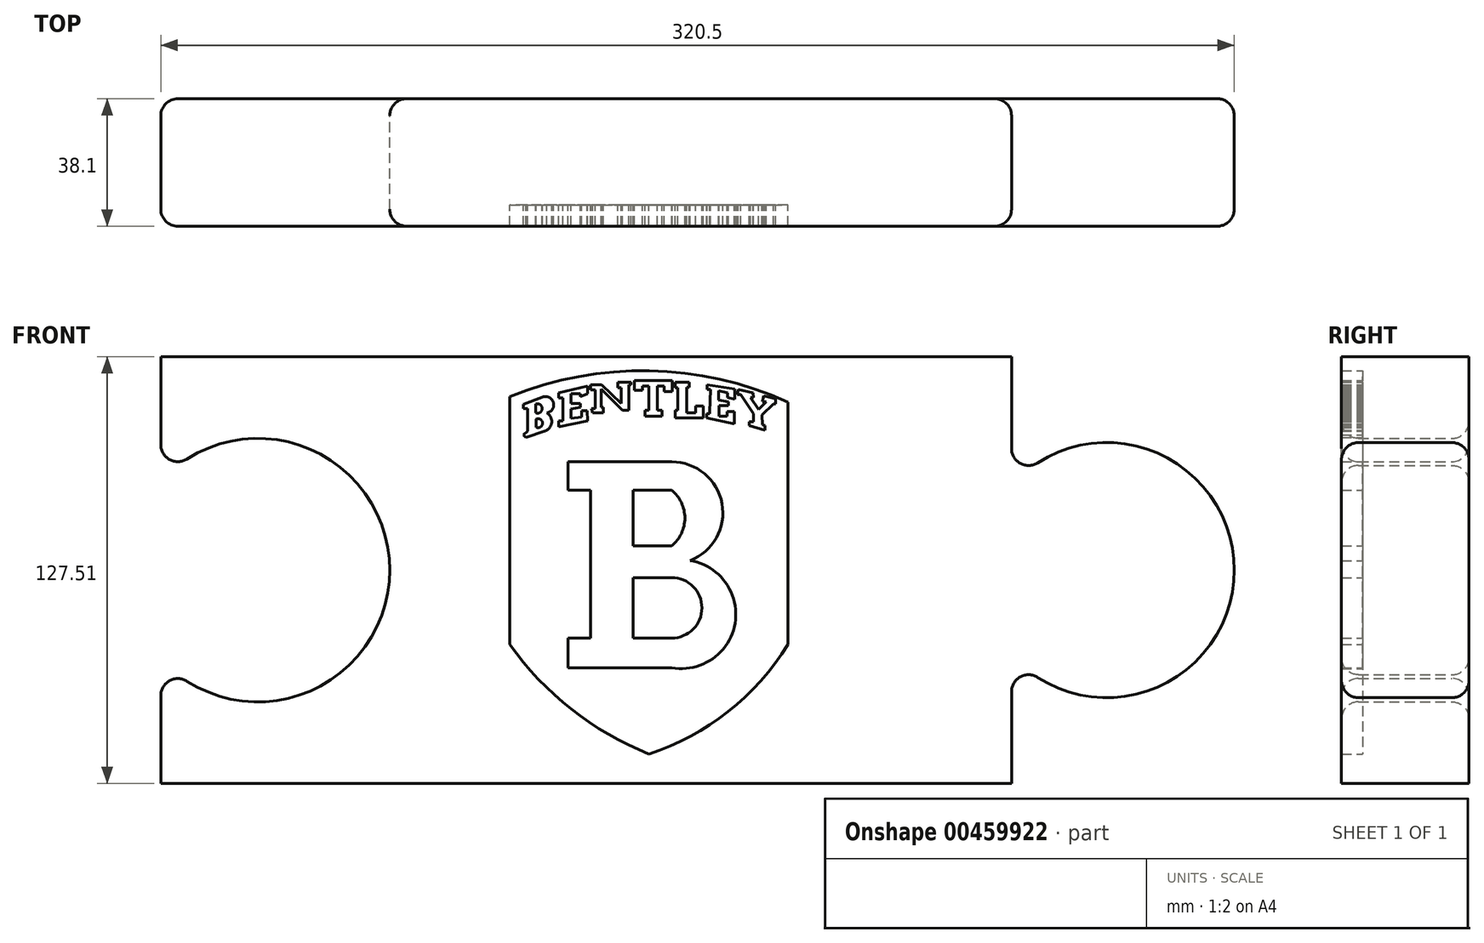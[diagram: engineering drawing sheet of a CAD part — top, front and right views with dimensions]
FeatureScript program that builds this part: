
annotation { "Feature Type Name" : "Feature", "Feature Type Description" : "" }
export const myFeature = defineFeature(function(context is Context, id is Id, definition is map)
    precondition{}
    {
        {
            var Q0;
            Q0=qCreatedBy(makeId("Front.planeOp"),FACE);
            var sketch = newSketch(context, id + "F0", { "sketchPlane" : qUnion([Q0])});
            skLineSegment(sketch, "E0", {"start": v(209.2, -174.77) * mm, "end": v(463.2, -174.77) * mm});
            skLineSegment(sketch, "E1", {"start": v(209.2, -302.28) * mm, "end": v(463.2, -302.28) * mm});
            skArc(sketch, "E2", {"start": v(463.2, -263.93) * mm, "mid": v(529.7, -238.53) * mm, "end": v(463.2, -213.13) * mm});
            skLineSegment(sketch, "E3", {"start": v(463.2, -213.13) * mm, "end": v(463.2, -174.77) * mm});
            skLineSegment(sketch, "E4", {"start": v(463.2, -263.93) * mm, "end": v(463.2, -302.28) * mm});
            skArc(sketch, "E5", {"start": v(209.2, -265.2) * mm, "mid": v(277.52, -238.53) * mm, "end": v(209.2, -211.86) * mm});
            skLineSegment(sketch, "E6", {"start": v(209.2, -265.2) * mm, "end": v(209.2, -302.28) * mm});
            skLineSegment(sketch, "E7", {"start": v(209.2, -211.86) * mm, "end": v(209.2, -174.77) * mm});
            skLineSegment(sketch, "E8", {"start": v(313.38, -186.66) * mm, "end": v(313.38, -260.76) * mm});
            skLineSegment(sketch, "E9", {"start": v(396.41, -188.31) * mm, "end": v(396.41, -260.76) * mm});
            skArc(sketch, "E10", {"start": v(396.41, -188.31) * mm, "mid": v(355.06, -178.97) * mm, "end": v(313.38, -186.66) * mm});
            skArc(sketch, "E11", {"start": v(313.38, -260.76) * mm, "mid": v(331.78, -280.1) * mm, "end": v(354.9, -293.46) * mm});
            skArc(sketch, "E12", {"start": v(354.9, -293.46) * mm, "mid": v(378.58, -280.83) * mm, "end": v(396.41, -260.76) * mm});
            skLineSegment(sketch, "E13", {"start": v(330.94, -206.94) * mm, "end": v(330.94, -216.88) * mm});
            skLineSegment(sketch, "E14", {"start": v(330.94, -206.94) * mm, "end": v(362.4, -206.94) * mm});
            skLineSegment(sketch, "E15", {"start": v(330.94, -216.88) * mm, "end": v(337.57, -216.88) * mm});
            skLineSegment(sketch, "E16", {"start": v(337.57, -216.88) * mm, "end": v(337.57, -259.1) * mm});
            skLineSegment(sketch, "E17", {"start": v(337.57, -259.1) * mm, "end": v(330.94, -259.1) * mm});
            skLineSegment(sketch, "E18", {"start": v(330.94, -259.1) * mm, "end": v(330.94, -269.04) * mm});
            skLineSegment(sketch, "E19", {"start": v(330.94, -269.04) * mm, "end": v(365.3, -269.04) * mm});
            skLineSegment(sketch, "E20", {"start": v(350.4, -241.72) * mm, "end": v(350.4, -258.62) * mm});
            skLineSegment(sketch, "E21", {"start": v(350.4, -241.72) * mm, "end": v(359.92, -241.72) * mm});
            skLineSegment(sketch, "E22", {"start": v(350.4, -215.64) * mm, "end": v(350.4, -230.95) * mm});
            skLineSegment(sketch, "E23", {"start": v(350.4, -215.64) * mm, "end": v(359.92, -215.64) * mm});
            skLineSegment(sketch, "E24", {"start": v(350.4, -230.95) * mm, "end": v(359.92, -230.95) * mm});
            skArc(sketch, "E25", {"start": v(359.92, -230.95) * mm, "mid": v(367.58, -223.3) * mm, "end": v(359.92, -215.64) * mm});
            skArc(sketch, "E26", {"start": v(359.92, -258.62) * mm, "mid": v(368.37, -250.17) * mm, "end": v(359.92, -241.72) * mm});
            skArc(sketch, "E27", {"start": v(366.54, -235.5) * mm, "mid": v(376.84, -219.43) * mm, "end": v(362.4, -206.94) * mm});
            skArc(sketch, "E28", {"start": v(365.3, -269.04) * mm, "mid": v(382.08, -252.87) * mm, "end": v(366.54, -235.5) * mm});
            skLineSegment(sketch, "E29", {"start": v(350.4, -258.62) * mm, "end": v(359.92, -258.62) * mm});
            skSolve(sketch);
        }
        {
            var Q0;
            Q0 = qSketchRegion(id + "F0", true);
            extrude(context, id + "F1", {"entities" : qUnion([Q0]), "depth" : 38.1 * mm});
        }
        {
            var Q0;
            Q0=makeQuery(id+"F1.opExtrude","CAP_FACE",FACE,{"disambiguationData":[OSD([sQuery(id+"F0.wireOp",EDGE,"E0"),sQuery(id+"F0.wireOp",EDGE,"E1"),sQuery(id+"F0.wireOp",EDGE,"E2"),sQuery(id+"F0.wireOp",EDGE,"E3"),sQuery(id+"F0.wireOp",EDGE,"E4"),sQuery(id+"F0.wireOp",EDGE,"E5"),sQuery(id+"F0.wireOp",EDGE,"E6"),sQuery(id+"F0.wireOp",EDGE,"E7")])],"isStart":false});
            var sketch = newSketch(context, id + "F2", { "sketchPlane" : qUnion([Q0])});
            skLineSegment(sketch, "E30", {"start": v(318.73, -148.22) * mm, "end": v(318.73, -266.2) * mm});
            skLineSegment(sketch, "E31", {"start": v(401.76, -149.36) * mm, "end": v(401.76, -266.2) * mm});
            skArc(sketch, "E32", {"start": v(401.76, -149.36) * mm, "mid": v(360.33, -142.8) * mm, "end": v(318.73, -148.22) * mm});
            skArc(sketch, "E33", {"start": v(318.73, -266.2) * mm, "mid": v(337.13, -285.54) * mm, "end": v(360.24, -298.9) * mm});
            skPoint(sketch, "E33.endSnap0", {"position": v(360.24, -302.28) * mm});
            skArc(sketch, "E34", {"start": v(360.24, -298.9) * mm, "mid": v(383.93, -286.26) * mm, "end": v(401.76, -266.2) * mm});
            skLineSegment(sketch, "E35", {"start": v(336.3, -212.38) * mm, "end": v(336.3, -222.32) * mm});
            skLineSegment(sketch, "E36", {"start": v(336.3, -212.38) * mm, "end": v(367.75, -212.38) * mm});
            skLineSegment(sketch, "E37", {"start": v(336.3, -222.32) * mm, "end": v(342.92, -222.32) * mm});
            skLineSegment(sketch, "E38", {"start": v(342.92, -222.32) * mm, "end": v(342.92, -264.54) * mm});
            skLineSegment(sketch, "E39", {"start": v(342.92, -264.54) * mm, "end": v(336.3, -264.54) * mm});
            skLineSegment(sketch, "E40", {"start": v(336.3, -264.54) * mm, "end": v(336.3, -274.48) * mm});
            skLineSegment(sketch, "E41", {"start": v(336.3, -274.48) * mm, "end": v(370.65, -274.48) * mm});
            skLineSegment(sketch, "E42", {"start": v(355.75, -248.3) * mm, "end": v(355.75, -265.2) * mm});
            skLineSegment(sketch, "E43", {"start": v(355.75, -248.3) * mm, "end": v(365.28, -248.3) * mm});
            skLineSegment(sketch, "E44", {"start": v(355.75, -222.22) * mm, "end": v(355.75, -237.53) * mm});
            skLineSegment(sketch, "E45", {"start": v(355.75, -222.22) * mm, "end": v(365.28, -222.22) * mm});
            skLineSegment(sketch, "E46", {"start": v(355.75, -237.53) * mm, "end": v(365.28, -237.53) * mm});
            skArc(sketch, "E47", {"start": v(365.28, -237.53) * mm, "mid": v(372.93, -229.88) * mm, "end": v(365.28, -222.22) * mm});
            skArc(sketch, "E48", {"start": v(365.28, -265.2) * mm, "mid": v(373.72, -256.75) * mm, "end": v(365.28, -248.3) * mm});
            skArc(sketch, "E49", {"start": v(371.9, -240.95) * mm, "mid": v(382.19, -224.87) * mm, "end": v(367.75, -212.38) * mm});
            skArc(sketch, "E50", {"start": v(370.65, -274.48) * mm, "mid": v(387.43, -258.3) * mm, "end": v(371.9, -240.95) * mm});
            skLineSegment(sketch, "E51", {"start": v(355.75, -265.2) * mm, "end": v(365.28, -265.2) * mm});
            skSolve(sketch);
        }
        {
            var Q0;
            Q0=makeQuery(id+"F0.imprint","IMPRINT",FACE,{"disambiguationData":[TD([[makeQuery(id+"F0.imprint","IMPRINT",EDGE,{"derivedFrom":sQuery(id+"F0.wireOp",EDGE,"E0")}),-1.0]])]});
            var sketch = newSketch(context, id + "F3", { "sketchPlane" : qUnion([Q0])});
            skLineSegment(sketch, "E52.bottom", {"start": v(409.93, -178.57) * mm, "end": v(283.82, -178.57) * mm});
            skLineSegment(sketch, "E52.top", {"start": v(409.93, -293.67) * mm, "end": v(283.82, -293.67) * mm});
            skLineSegment(sketch, "E52.left", {"start": v(409.93, -178.57) * mm, "end": v(409.93, -293.67) * mm});
            skLineSegment(sketch, "E52.right", {"start": v(283.82, -178.57) * mm, "end": v(283.82, -293.67) * mm});
            skSolve(sketch);
        }
        {
            var Q0;
            Q0 = qSketchRegion(id + "F3", true);
            extrude(context, id + "F4", {"entities" : qUnion([Q0]), "operationType" : NewBodyOperationType.ADD, "depth" : 31.75 * mm});
        }
        {
            var Q0;
            Q0=makeQuery(id+"F4.opExtrude","CAP_FACE",FACE,{"disambiguationData":[OSD([sQuery(id+"F3.wireOp",EDGE,"E52.bottom"),sQuery(id+"F3.wireOp",EDGE,"E52.top"),sQuery(id+"F3.wireOp",EDGE,"E52.left"),sQuery(id+"F3.wireOp",EDGE,"E52.right")])],"isStart":false});
            var sketch = newSketch(context, id + "F5", { "sketchPlane" : qUnion([Q0])});
            skLineSegment(sketch, "E53", {"start": v(330.82, -206.17) * mm, "end": v(330.82, -214.68) * mm});
            skLineSegment(sketch, "E54", {"start": v(330.82, -214.68) * mm, "end": v(337.54, -214.68) * mm});
            skLineSegment(sketch, "E55", {"start": v(337.54, -214.68) * mm, "end": v(337.54, -258.85) * mm});
            skLineSegment(sketch, "E56", {"start": v(337.54, -258.85) * mm, "end": v(330.82, -258.85) * mm});
            skLineSegment(sketch, "E57", {"start": v(330.82, -258.85) * mm, "end": v(330.82, -267.7) * mm});
            skLineSegment(sketch, "E58", {"start": v(330.82, -267.7) * mm, "end": v(361.73, -267.7) * mm});
            skLineSegment(sketch, "E59", {"start": v(330.82, -206.17) * mm, "end": v(361.73, -206.17) * mm});
            skLineSegment(sketch, "E60", {"start": v(350.15, -214.68) * mm, "end": v(350.15, -231.25) * mm});
            skLineSegment(sketch, "E61", {"start": v(350.15, -240.8) * mm, "end": v(350.15, -258.85) * mm});
            skLineSegment(sketch, "E62", {"start": v(350.15, -240.8) * mm, "end": v(361.73, -240.8) * mm});
            skLineSegment(sketch, "E63", {"start": v(350.15, -258.85) * mm, "end": v(361.73, -258.85) * mm});
            skLineSegment(sketch, "E64", {"start": v(350.15, -214.68) * mm, "end": v(361.73, -214.68) * mm});
            skLineSegment(sketch, "E65", {"start": v(350.15, -231.25) * mm, "end": v(361.73, -231.25) * mm});
            skArc(sketch, "E66", {"start": v(361.73, -231.25) * mm, "mid": v(365.65, -222.97) * mm, "end": v(361.73, -214.68) * mm});
            skArc(sketch, "E67", {"start": v(361.73, -258.85) * mm, "mid": v(370.76, -249.82) * mm, "end": v(361.73, -240.8) * mm});
            skArc(sketch, "E68", {"start": v(361.73, -267.7) * mm, "mid": v(380.62, -254.45) * mm, "end": v(367.18, -235.68) * mm});
            skArc(sketch, "E69", {"start": v(367.18, -235.68) * mm, "mid": v(376.74, -218.66) * mm, "end": v(361.73, -206.17) * mm});
            skLineSegment(sketch, "E70", {"start": v(317.46, -188.92) * mm, "end": v(317.46, -190.3) * mm});
            skLineSegment(sketch, "E71", {"start": v(317.46, -190.3) * mm, "end": v(318.7, -190.3) * mm});
            skLineSegment(sketch, "E72", {"start": v(318.7, -190.3) * mm, "end": v(318.7, -197.02) * mm});
            skLineSegment(sketch, "E73", {"start": v(318.7, -197.02) * mm, "end": v(317.46, -198.15) * mm});
            skLineSegment(sketch, "E74", {"start": v(317.46, -198.15) * mm, "end": v(318.14, -198.9) * mm});
            skLineSegment(sketch, "E75", {"start": v(318.14, -198.9) * mm, "end": v(323.82, -197.02) * mm});
            skLineSegment(sketch, "E76", {"start": v(317.46, -188.92) * mm, "end": v(323.2, -186.8) * mm});
            skArc(sketch, "E77", {"start": v(324.44, -191.54) * mm, "mid": v(326.43, -188.49) * mm, "end": v(323.2, -186.8) * mm});
            skArc(sketch, "E78", {"start": v(323.82, -197.02) * mm, "mid": v(325.89, -194.48) * mm, "end": v(324.44, -191.54) * mm});
            skLineSegment(sketch, "E79", {"start": v(321.1, -188.9) * mm, "end": v(321.1, -191.55) * mm});
            skLineSegment(sketch, "E80", {"start": v(321.27, -193.4) * mm, "end": v(321.27, -195.84) * mm});
            skArc(sketch, "E81", {"start": v(321.1, -191.55) * mm, "mid": v(323.05, -190.23) * mm, "end": v(321.1, -188.9) * mm});
            skArc(sketch, "E82", {"start": v(321.27, -195.84) * mm, "mid": v(323.18, -194.62) * mm, "end": v(321.27, -193.4) * mm});
            skLineSegment(sketch, "E83", {"start": v(327.92, -185.54) * mm, "end": v(327.92, -187.12) * mm});
            skLineSegment(sketch, "E84", {"start": v(327.92, -187.12) * mm, "end": v(329.22, -187.12) * mm});
            skLineSegment(sketch, "E85", {"start": v(329.22, -187.12) * mm, "end": v(329.22, -193.95) * mm});
            skLineSegment(sketch, "E86", {"start": v(329.22, -193.95) * mm, "end": v(327.92, -193.95) * mm});
            skLineSegment(sketch, "E87", {"start": v(327.92, -193.95) * mm, "end": v(327.92, -195.7) * mm});
            skLineSegment(sketch, "E88", {"start": v(327.92, -195.7) * mm, "end": v(336.6, -193.95) * mm});
            skLineSegment(sketch, "E89", {"start": v(331.62, -186.66) * mm, "end": v(331.62, -185.82) * mm});
            skLineSegment(sketch, "E90", {"start": v(331.62, -185.82) * mm, "end": v(334.5, -185.82) * mm});
            skLineSegment(sketch, "E91", {"start": v(334.5, -185.82) * mm, "end": v(334.5, -186.66) * mm});
            skLineSegment(sketch, "E92", {"start": v(334.5, -186.66) * mm, "end": v(336.6, -185.82) * mm});
            skLineSegment(sketch, "E93", {"start": v(336.6, -185.82) * mm, "end": v(336.6, -183.51) * mm});
            skLineSegment(sketch, "E94", {"start": v(336.6, -183.51) * mm, "end": v(327.92, -185.54) * mm});
            skLineSegment(sketch, "E95", {"start": v(337.55, -183.12) * mm, "end": v(337.55, -184.67) * mm});
            skPoint(sketch, "E95.endSnap0", {"position": v(336.6, -184.67) * mm});
            skLineSegment(sketch, "E96", {"start": v(337.55, -184.67) * mm, "end": v(338.92, -184.67) * mm});
            skLineSegment(sketch, "E97", {"start": v(338.92, -184.67) * mm, "end": v(338.92, -190.24) * mm});
            skLineSegment(sketch, "E98", {"start": v(338.92, -190.24) * mm, "end": v(337.78, -190.24) * mm});
            skLineSegment(sketch, "E99", {"start": v(337.78, -190.24) * mm, "end": v(338.08, -191.54) * mm});
            skLineSegment(sketch, "E100", {"start": v(338.08, -191.54) * mm, "end": v(341.32, -191.54) * mm});
            skLineSegment(sketch, "E101", {"start": v(341.32, -191.54) * mm, "end": v(341.32, -189.93) * mm});
            skLineSegment(sketch, "E102", {"start": v(341.32, -189.93) * mm, "end": v(340.71, -189.93) * mm});
            skLineSegment(sketch, "E103", {"start": v(340.71, -189.93) * mm, "end": v(340.71, -184.45) * mm});
            skLineSegment(sketch, "E104", {"start": v(340.71, -184.45) * mm, "end": v(346.99, -190.73) * mm});
            skLineSegment(sketch, "E105", {"start": v(346.99, -190.73) * mm, "end": v(348.87, -190.73) * mm});
            skLineSegment(sketch, "E106", {"start": v(348.87, -190.73) * mm, "end": v(348.87, -183.16) * mm});
            skLineSegment(sketch, "E107", {"start": v(348.87, -183.16) * mm, "end": v(349.6, -183.16) * mm});
            skLineSegment(sketch, "E108", {"start": v(349.6, -183.16) * mm, "end": v(349.6, -182.36) * mm});
            skLineSegment(sketch, "E109", {"start": v(349.6, -182.36) * mm, "end": v(345.61, -182.36) * mm});
            skLineSegment(sketch, "E110", {"start": v(345.61, -182.36) * mm, "end": v(345.61, -184.07) * mm});
            skLineSegment(sketch, "E111", {"start": v(345.61, -184.07) * mm, "end": v(346.58, -184.07) * mm});
            skLineSegment(sketch, "E112", {"start": v(346.58, -184.07) * mm, "end": v(346.58, -188.74) * mm});
            skLineSegment(sketch, "E113", {"start": v(346.58, -188.74) * mm, "end": v(340.77, -183.16) * mm});
            skLineSegment(sketch, "E114", {"start": v(340.77, -183.16) * mm, "end": v(337.55, -183.12) * mm});
            skLineSegment(sketch, "E115", {"start": v(350.6, -182.34) * mm, "end": v(350.6, -184.74) * mm});
            skLineSegment(sketch, "E116", {"start": v(350.6, -184.74) * mm, "end": v(352.95, -184.74) * mm});
            skLineSegment(sketch, "E117", {"start": v(352.95, -184.79) * mm, "end": v(352.95, -183.56) * mm});
            skLineSegment(sketch, "E118", {"start": v(352.95, -183.56) * mm, "end": v(354.88, -183.56) * mm});
            skLineSegment(sketch, "E119", {"start": v(354.88, -183.56) * mm, "end": v(354.88, -190.76) * mm});
            skLineSegment(sketch, "E120", {"start": v(354.88, -190.76) * mm, "end": v(353.8, -190.76) * mm});
            skLineSegment(sketch, "E121", {"start": v(353.8, -190.76) * mm, "end": v(353.8, -192.6) * mm});
            skLineSegment(sketch, "E122", {"start": v(353.8, -192.6) * mm, "end": v(358.78, -192.6) * mm});
            skLineSegment(sketch, "E123", {"start": v(358.78, -192.6) * mm, "end": v(358.78, -190.76) * mm});
            skLineSegment(sketch, "E124", {"start": v(358.78, -190.76) * mm, "end": v(357.47, -190.76) * mm});
            skLineSegment(sketch, "E125", {"start": v(357.47, -190.76) * mm, "end": v(357.47, -183.56) * mm});
            skLineSegment(sketch, "E126", {"start": v(357.47, -183.56) * mm, "end": v(359.5, -183.56) * mm});
            skLineSegment(sketch, "E127", {"start": v(359.5, -183.56) * mm, "end": v(359.5, -185.12) * mm});
            skLineSegment(sketch, "E128", {"start": v(359.5, -185.12) * mm, "end": v(361.89, -185.12) * mm});
            skLineSegment(sketch, "E129", {"start": v(361.89, -185.12) * mm, "end": v(361.89, -181.82) * mm});
            skLineSegment(sketch, "E130", {"start": v(361.89, -181.82) * mm, "end": v(350.6, -181.82) * mm});
            skLineSegment(sketch, "E131", {"start": v(350.6, -182.34) * mm, "end": v(350.6, -181.82) * mm});
            skLineSegment(sketch, "E132", {"start": v(363.5, -190.76) * mm, "end": v(362.71, -190.76) * mm});
            skLineSegment(sketch, "E133", {"start": v(362.71, -190.76) * mm, "end": v(362.71, -193.02) * mm});
            skLineSegment(sketch, "E134", {"start": v(362.71, -193.02) * mm, "end": v(371.14, -193.02) * mm});
            skLineSegment(sketch, "E135", {"start": v(371.14, -193.02) * mm, "end": v(371.14, -189.48) * mm});
            skLineSegment(sketch, "E136", {"start": v(371.14, -189.48) * mm, "end": v(368.8, -189.48) * mm});
            skLineSegment(sketch, "E137", {"start": v(368.8, -189.48) * mm, "end": v(368.8, -191.48) * mm});
            skLineSegment(sketch, "E138", {"start": v(368.8, -191.48) * mm, "end": v(366.18, -191.48) * mm});
            skLineSegment(sketch, "E139", {"start": v(366.18, -191.48) * mm, "end": v(366.18, -183.88) * mm});
            skLineSegment(sketch, "E140", {"start": v(366.18, -183.88) * mm, "end": v(367.01, -183.88) * mm});
            skLineSegment(sketch, "E141", {"start": v(367.01, -183.88) * mm, "end": v(367.01, -182.34) * mm});
            skLineSegment(sketch, "E142", {"start": v(367.01, -182.34) * mm, "end": v(362.71, -182.34) * mm});
            skLineSegment(sketch, "E143", {"start": v(362.71, -182.34) * mm, "end": v(362.71, -184.05) * mm});
            skLineSegment(sketch, "E144", {"start": v(362.71, -184.05) * mm, "end": v(363.5, -184.05) * mm});
            skLineSegment(sketch, "E145", {"start": v(363.5, -184.05) * mm, "end": v(363.5, -190.76) * mm});
            skLineSegment(sketch, "E146", {"start": v(373.01, -191.73) * mm, "end": v(372.17, -191.73) * mm});
            skLineSegment(sketch, "E147", {"start": v(372.17, -191.73) * mm, "end": v(372.17, -193.05) * mm});
            skLineSegment(sketch, "E148", {"start": v(372.17, -193.05) * mm, "end": v(380.44, -194.79) * mm});
            skLineSegment(sketch, "E149", {"start": v(380.44, -194.79) * mm, "end": v(380.44, -191.2) * mm});
            skLineSegment(sketch, "E150", {"start": v(380.44, -191.2) * mm, "end": v(378.23, -191.2) * mm});
            skLineSegment(sketch, "E151", {"start": v(378.23, -191.2) * mm, "end": v(378.23, -192.57) * mm});
            skLineSegment(sketch, "E152", {"start": v(378.23, -192.57) * mm, "end": v(375.83, -192.57) * mm});
            skLineSegment(sketch, "E153", {"start": v(375.83, -192.57) * mm, "end": v(375.83, -189.4) * mm});
            skLineSegment(sketch, "E154", {"start": v(375.83, -189.4) * mm, "end": v(378.65, -189.4) * mm});
            skLineSegment(sketch, "E155", {"start": v(378.65, -189.4) * mm, "end": v(378.65, -188.2) * mm});
            skLineSegment(sketch, "E156", {"start": v(378.65, -188.2) * mm, "end": v(375.77, -187.66) * mm});
            skLineSegment(sketch, "E157", {"start": v(375.77, -187.66) * mm, "end": v(375.77, -184.9) * mm});
            skLineSegment(sketch, "E158", {"start": v(375.77, -184.9) * mm, "end": v(378.35, -185.56) * mm});
            skLineSegment(sketch, "E159", {"start": v(378.35, -185.56) * mm, "end": v(378.35, -186.94) * mm});
            skLineSegment(sketch, "E160", {"start": v(378.35, -186.94) * mm, "end": v(380.56, -187.48) * mm});
            skLineSegment(sketch, "E161", {"start": v(380.56, -187.48) * mm, "end": v(380.56, -184.36) * mm});
            skLineSegment(sketch, "E162", {"start": v(380.56, -184.36) * mm, "end": v(372.35, -183.16) * mm});
            skLineSegment(sketch, "E163", {"start": v(372.35, -183.16) * mm, "end": v(372.35, -184.48) * mm});
            skLineSegment(sketch, "E164", {"start": v(372.35, -184.48) * mm, "end": v(373.37, -184.48) * mm});
            skLineSegment(sketch, "E165", {"start": v(373.37, -184.48) * mm, "end": v(373.01, -191.25) * mm});
            skLineSegment(sketch, "E166", {"start": v(373.01, -191.25) * mm, "end": v(373.01, -191.73) * mm});
            skLineSegment(sketch, "E167", {"start": v(381.28, -186.04) * mm, "end": v(382.3, -186.04) * mm});
            skLineSegment(sketch, "E168", {"start": v(382.3, -186.04) * mm, "end": v(386.14, -191.73) * mm});
            skLineSegment(sketch, "E169", {"start": v(386.14, -191.73) * mm, "end": v(386.14, -194.13) * mm});
            skLineSegment(sketch, "E170", {"start": v(386.14, -194.13) * mm, "end": v(384.82, -194.13) * mm});
            skLineSegment(sketch, "E171", {"start": v(384.82, -194.13) * mm, "end": v(384.82, -195.39) * mm});
            skLineSegment(sketch, "E172", {"start": v(384.82, -195.39) * mm, "end": v(389.55, -196.7) * mm});
            skLineSegment(sketch, "E173", {"start": v(389.55, -196.7) * mm, "end": v(389.55, -195.33) * mm});
            skLineSegment(sketch, "E174", {"start": v(389.55, -195.33) * mm, "end": v(388.78, -195.09) * mm});
            skLineSegment(sketch, "E175", {"start": v(388.78, -195.09) * mm, "end": v(388.72, -192.21) * mm});
            skLineSegment(sketch, "E176", {"start": v(388.72, -192.21) * mm, "end": v(392.13, -188.86) * mm});
            skLineSegment(sketch, "E177", {"start": v(392.13, -188.86) * mm, "end": v(392.8, -188.86) * mm});
            skLineSegment(sketch, "E178", {"start": v(392.8, -188.86) * mm, "end": v(392.8, -187.3) * mm});
            skLineSegment(sketch, "E179", {"start": v(392.8, -187.3) * mm, "end": v(389.14, -186.46) * mm});
            skLineSegment(sketch, "E180", {"start": v(389.14, -186.46) * mm, "end": v(388.84, -188.2) * mm});
            skLineSegment(sketch, "E181", {"start": v(388.84, -188.2) * mm, "end": v(389.97, -188.2) * mm});
            skLineSegment(sketch, "E182", {"start": v(389.97, -188.2) * mm, "end": v(387.64, -190.53) * mm});
            skLineSegment(sketch, "E183", {"start": v(387.64, -190.53) * mm, "end": v(385.24, -186.94) * mm});
            skLineSegment(sketch, "E184", {"start": v(385.24, -186.94) * mm, "end": v(386.14, -186.94) * mm});
            skLineSegment(sketch, "E185", {"start": v(386.14, -186.94) * mm, "end": v(385.96, -185.5) * mm});
            skLineSegment(sketch, "E186", {"start": v(385.96, -185.5) * mm, "end": v(381.58, -184.6) * mm});
            skLineSegment(sketch, "E187", {"start": v(381.58, -184.6) * mm, "end": v(381.28, -186.04) * mm});
            skLineSegment(sketch, "E188", {"start": v(331.62, -186.66) * mm, "end": v(331.62, -188.67) * mm});
            skLineSegment(sketch, "E189", {"start": v(331.62, -188.67) * mm, "end": v(334.46, -188.67) * mm});
            skLineSegment(sketch, "E190", {"start": v(334.46, -188.67) * mm, "end": v(334.46, -189.86) * mm});
            skLineSegment(sketch, "E191", {"start": v(334.46, -189.86) * mm, "end": v(331.62, -190.42) * mm});
            skLineSegment(sketch, "E192", {"start": v(331.62, -190.42) * mm, "end": v(331.62, -193.24) * mm});
            skLineSegment(sketch, "E193", {"start": v(331.62, -193.24) * mm, "end": v(334.78, -192.79) * mm});
            skLineSegment(sketch, "E194", {"start": v(334.78, -192.79) * mm, "end": v(334.78, -190.87) * mm});
            skLineSegment(sketch, "E195", {"start": v(334.78, -190.87) * mm, "end": v(336.55, -190.87) * mm});
            skLineSegment(sketch, "E196", {"start": v(336.55, -190.87) * mm, "end": v(336.6, -193.95) * mm});
            skSolve(sketch);
        }
        {
            var Q0;
            Q0 = qSketchRegion(id + "F5", true);
            extrude(context, id + "F6", {"entities" : qUnion([Q0]), "operationType" : NewBodyOperationType.ADD, "depth" : 6.35 * mm});
        }
        {
            var Q0;
            Q0=makeQuery(id+"F1.opExtrude","CAP_EDGE",EDGE,{"disambiguationData":[OSD([sQuery(id+"F0.wireOp",EDGE,"E5")])],"isStart":false});
            var Q1;
            Q1=makeQuery(id+"F1.opExtrude","CAP_EDGE",EDGE,{"disambiguationData":[OSD([sQuery(id+"F0.wireOp",EDGE,"E7")])],"isStart":false});
            var Q2;
            Q2=makeQuery(id+"F1.opExtrude","CAP_EDGE",EDGE,{"disambiguationData":[OSD([sQuery(id+"F0.wireOp",EDGE,"E6")])],"isStart":false});
            var Q3;
            Q3=makeQuery(id+"F1.opExtrude","SWEPT_EDGE",EDGE,{"disambiguationData":[OSD([sQuery(id+"F0.wireOp",EDGE,"E5"),sQuery(id+"F0.wireOp",EDGE,"E7")])]});
            var Q4;
            Q4=makeQuery(id+"F1.opExtrude","SWEPT_EDGE",EDGE,{"disambiguationData":[OSD([sQuery(id+"F0.wireOp",EDGE,"E5"),sQuery(id+"F0.wireOp",EDGE,"E6")])]});
            var Q5;
            Q5=makeQuery(id+"F1.opExtrude","CAP_EDGE",EDGE,{"disambiguationData":[OSD([sQuery(id+"F0.wireOp",EDGE,"E7")])],"isStart":true});
            var Q6;
            Q6=makeQuery(id+"F1.opExtrude","CAP_EDGE",EDGE,{"disambiguationData":[OSD([sQuery(id+"F0.wireOp",EDGE,"E6")])],"isStart":true});
            var Q7;
            Q7=makeQuery(id+"F1.opExtrude","SWEPT_FACE",FACE,{"disambiguationData":[OSD([sQuery(id+"F0.wireOp",EDGE,"E5")])]});
            fillet(context, id + "F7", {"entities" : qUnion([Q0, Q1, Q2, Q3, Q4, Q5, Q6, Q7]), "radius" : 5.08 * mm, "tangentPropagation" : true, "allowEdgeOverflow" : false});
        }
        {
            var Q0;
            Q0=makeQuery(id+"F1.opExtrude","CAP_EDGE",EDGE,{"disambiguationData":[OSD([sQuery(id+"F0.wireOp",EDGE,"E2")])],"isStart":false});
            var Q1;
            Q1=makeQuery(id+"F1.opExtrude","CAP_EDGE",EDGE,{"disambiguationData":[OSD([sQuery(id+"F0.wireOp",EDGE,"E3")])],"isStart":false});
            var Q2;
            Q2=makeQuery(id+"F1.opExtrude","CAP_EDGE",EDGE,{"disambiguationData":[OSD([sQuery(id+"F0.wireOp",EDGE,"E3")])],"isStart":true});
            var Q3;
            Q3=makeQuery(id+"F1.opExtrude","CAP_EDGE",EDGE,{"disambiguationData":[OSD([sQuery(id+"F0.wireOp",EDGE,"E4")])],"isStart":false});
            var Q4;
            Q4=makeQuery(id+"F1.opExtrude","CAP_EDGE",EDGE,{"disambiguationData":[OSD([sQuery(id+"F0.wireOp",EDGE,"E4")])],"isStart":true});
            var Q5;
            Q5=makeQuery(id+"F1.opExtrude","SWEPT_EDGE",EDGE,{"disambiguationData":[OSD([sQuery(id+"F0.wireOp",EDGE,"E2"),sQuery(id+"F0.wireOp",EDGE,"E3")])]});
            var Q6;
            Q6=makeQuery(id+"F1.opExtrude","CAP_EDGE",EDGE,{"disambiguationData":[OSD([sQuery(id+"F0.wireOp",EDGE,"E2")])],"isStart":true});
            var Q7;
            Q7=makeQuery(id+"F1.opExtrude","SWEPT_FACE",FACE,{"disambiguationData":[OSD([sQuery(id+"F0.wireOp",EDGE,"E2")])]});
            fillet(context, id + "F8", {"entities" : qUnion([Q0, Q1, Q2, Q3, Q4, Q5, Q6, Q7]), "radius" : 5.08 * mm, "tangentPropagation" : true, "allowEdgeOverflow" : false});
        }
    });
